# Revit family: QF_Vollrath_36404HD_cat
name_source: partatom
category: Specialty Equipment
revit_build: Autodesk Revit 2016 (Build: 20151007_0715(x64)
units: mm (PartAtom-declared; Revit-internal decimal feet)

## family parameters
Always vertical = Yes
Cut with Voids When Loaded = Yes
OmniClass Number = 23.40.40.11.31
OmniClass Title = Steam Tables
Part Type = Normal
Room Calculation Point = No
Round Connector Dimension = Use Diameter
Shared = No
Work Plane-Based = Yes

## types (1)
- QF_Vollrath_36404HD_cat
    Apparent Power = 0 VA
    Conn Conduit = Yes
    Conn Plug = NEMA 5-15P
    Cycle = 60 Hz
    Default Elevation = 48"
    Depth = 26"
    Description = Drop-In, Hot
    Elec Conn Connection Height = 0"
    FL Amps = 0 A
    Foodservice Equipment Identifier = Yes
    Height = 15"
    Indirect Waste Connection Height = 0"
    Indirect Waste Size = 1"
    Manifold Drain = No
    Manufacturer = Vollrath
    Max Overcurrent Protection = 0 A
    Min Ckt Ampacity = 0 A
    Model = -
    Phase = 1
    Plumbing Connection Type = -
    Volts = 0 V
    Watts = 0 W
    Weight in Pounds = 0
    Width = 41 1/2"

## geometry (parser evidence)
native form markers: Blend x30, Sweep x4
no freeform markers — native parametric forms only
